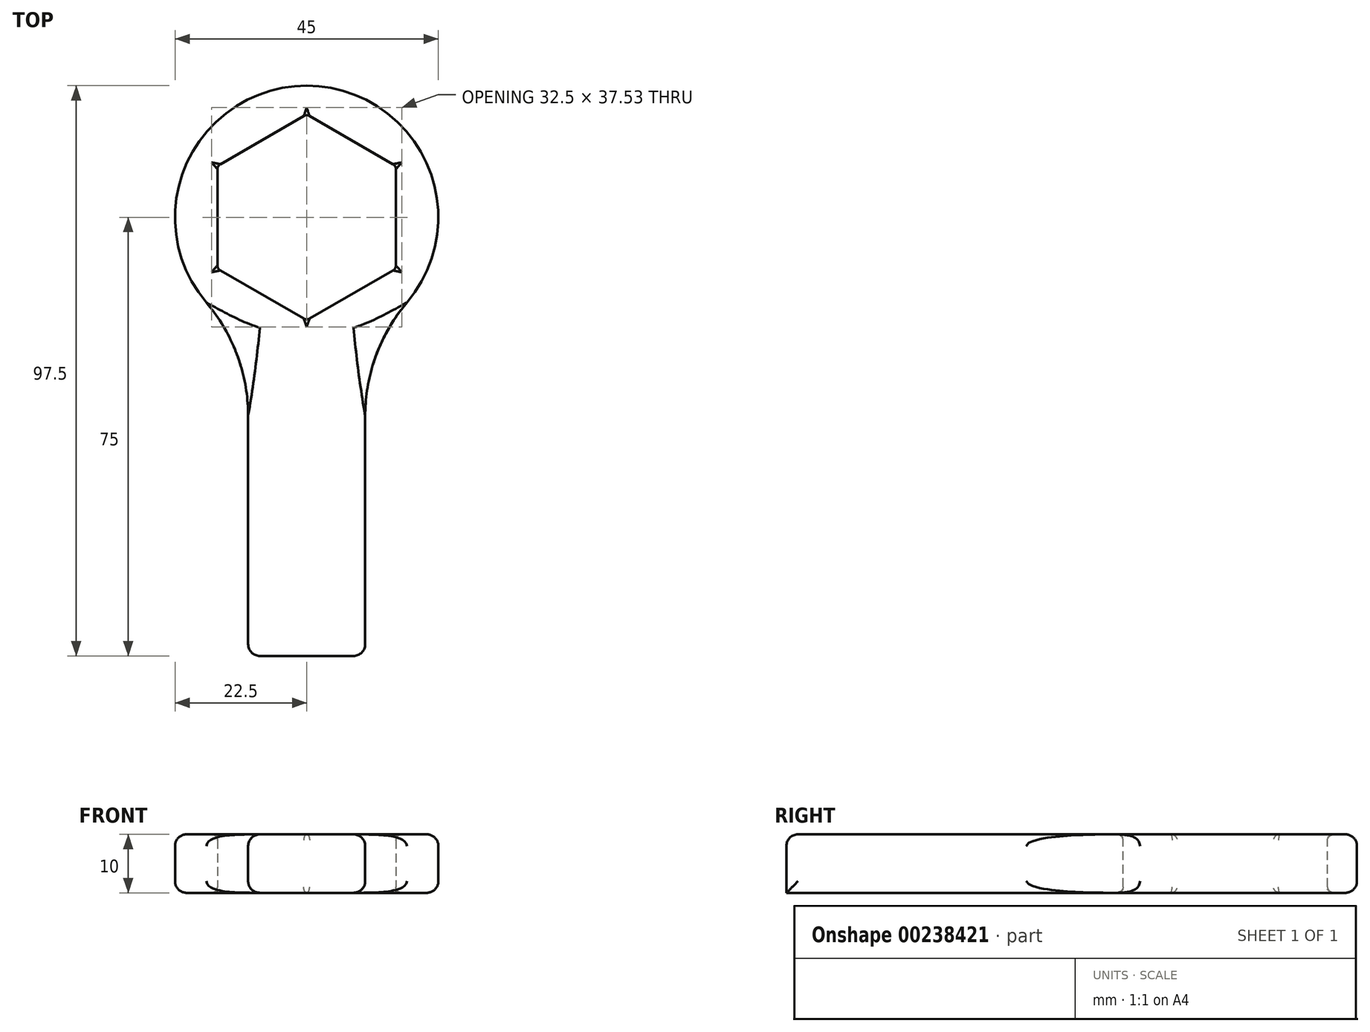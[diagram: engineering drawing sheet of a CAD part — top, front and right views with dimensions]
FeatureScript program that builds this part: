
annotation { "Feature Type Name" : "Feature", "Feature Type Description" : "" }
export const myFeature = defineFeature(function(context is Context, id is Id, definition is map)
    precondition{}
    {
        {
            var Q0;
            Q0=qCreatedBy(makeId("Top.planeOp"),FACE);
            var sketch = newSketch(context, id + "F0", { "sketchPlane" : qUnion([Q0])});
            skCircle(sketch, "E0.cCircle", {"center": v(0, 0) * mm, "radius": 15.25 * mm, "construction": true});
            skLineSegment(sketch, "E0.0", {"start": v(15.25, 8.8) * mm, "end": v(15.25, -8.8) * mm});
            skLineSegment(sketch, "E0.1", {"start": v(15.25, -8.8) * mm, "end": v(0, -17.6) * mm});
            skLineSegment(sketch, "E0.2", {"start": v(0, -17.6) * mm, "end": v(-15.25, -8.8) * mm});
            skLineSegment(sketch, "E0.3", {"start": v(-15.25, -8.8) * mm, "end": v(-15.25, 8.8) * mm});
            skLineSegment(sketch, "E0.4", {"start": v(-15.25, 8.8) * mm, "end": v(0, 17.6) * mm});
            skLineSegment(sketch, "E0.5", {"start": v(0, 17.6) * mm, "end": v(15.25, 8.8) * mm});
            skPoint(sketch, "E0.0.midPoint", {"position": v(15.25, 0) * mm});
            skCircle(sketch, "E1", {"center": v(0, 0) * mm, "radius": 22.5 * mm});
            skLineSegment(sketch, "E2.bottom", {"start": v(10, -75) * mm, "end": v(-10, -75) * mm});
            skLineSegment(sketch, "E2.top", {"start": v(10, 75) * mm, "end": v(-10, 75) * mm});
            skLineSegment(sketch, "E2.left", {"start": v(10, -75) * mm, "end": v(10, 75) * mm});
            skLineSegment(sketch, "E2.right", {"start": v(-10, -75) * mm, "end": v(-10, 75) * mm});
            skSolve(sketch);
        }
        {
            var Q0;
            {var subQ5=sQuery(id+"F0.wireOp",EDGE,"E2.bottom");Q0=makeQuery(id+"F0.imprint","IMPRINT",FACE,{"disambiguationData":[TD([[makeQuery(id+"F0.imprint","IMPRINT",EDGE,{"derivedFrom":subQ5}),-1.0]])]});}
            var Q1;
            {var subQ5=sQuery(id+"F0.wireOp",EDGE,"E0.0");Q1=makeQuery(id+"F0.imprint","IMPRINT",FACE,{"disambiguationData":[TD([[makeQuery(id+"F0.imprint","IMPRINT",EDGE,{"derivedFrom":subQ5}),1.0]])]});}
            var Q2;
            {var subQ7=sQuery(id+"F0.wireOp",EDGE,"E0.3");Q2=makeQuery(id+"F0.imprint","IMPRINT",FACE,{"disambiguationData":[TD([[makeQuery(id+"F0.imprint","IMPRINT",EDGE,{"derivedFrom":subQ7}),1.0]])]});}
            var Q3;
            {var subQ0=sQuery(id+"F0.wireOp",EDGE,"E0.2");var subQ1=sQuery(id+"F0.wireOp",EDGE,"E0.1");var subQ2=makeQuery(id+"F0.imprint","INTERSECT",VERTEX,{"derivedFrom":[subQ1,subQ0]});Q3=makeQuery(id+"F0.imprint","IMPRINT",FACE,{"disambiguationData":[TD([[makeQuery(id+"F0.imprint","IMPRINT",EDGE,{"disambiguationData":[TD([[subQ2,1.0]])],"derivedFrom":subQ1}),1.0]])]});}
            var Q4;
            {var subQ3=sQuery(id+"F0.wireOp",EDGE,"E0.5");var subQ5=sQuery(id+"F0.wireOp",EDGE,"E0.4");var subQ6=makeQuery(id+"F0.imprint","INTERSECT",VERTEX,{"derivedFrom":[subQ5,subQ3]});Q4=makeQuery(id+"F0.imprint","IMPRINT",FACE,{"disambiguationData":[TD([[makeQuery(id+"F0.imprint","IMPRINT",EDGE,{"disambiguationData":[TD([[subQ6,1.0]])],"derivedFrom":subQ5}),1.0]])]});}
            extrude(context, id + "F1", {"entities" : qUnion([Q0, Q1, Q2, Q3, Q4]), "depth" : 10 * mm, "offsetDistance" : 25 * mm});
        }
        {
            var Q0;
            Q0=makeQuery(id+"F1.opExtrude","CAP_EDGE",EDGE,{"disambiguationData":[OSD([sQuery(id+"F0.wireOp",EDGE,"E2.right")])],"isStart":false});
            var Q1;
            Q1=makeQuery(id+"F1.opExtrude","CAP_EDGE",EDGE,{"disambiguationData":[OSD([sQuery(id+"F0.wireOp",EDGE,"E2.left")])],"isStart":false});
            var Q2;
            Q2=makeQuery(id+"F1.opExtrude","CAP_EDGE",EDGE,{"disambiguationData":[OSD([sQuery(id+"F0.wireOp",EDGE,"E2.bottom")])],"isStart":false});
            var Q3;
            Q3=makeQuery(id+"F1.opExtrude","SWEPT_EDGE",EDGE,{"disambiguationData":[OSD([sQuery(id+"F0.wireOp",EDGE,"E2.bottom"),sQuery(id+"F0.wireOp",EDGE,"E2.right")])]});
            var Q4;
            Q4=makeQuery(id+"F1.opExtrude","SWEPT_EDGE",EDGE,{"disambiguationData":[OSD([sQuery(id+"F0.wireOp",EDGE,"E2.bottom"),sQuery(id+"F0.wireOp",EDGE,"E2.left")])]});
            var Q5;
            Q5=makeQuery(id+"F1.opExtrude","CAP_EDGE",EDGE,{"disambiguationData":[OSD([sQuery(id+"F0.wireOp",EDGE,"E2.right")])],"isStart":true});
            var Q6;
            Q6=makeQuery(id+"F1.opExtrude","CAP_EDGE",EDGE,{"disambiguationData":[OSD([sQuery(id+"F0.wireOp",EDGE,"E2.left")])],"isStart":true});
            fillet(context, id + "F2", {"entities" : qUnion([Q0, Q1, Q2, Q3, Q4, Q5, Q6]), "radius" : 2 * mm, "allowEdgeOverflow" : false});
        }
        {
            var Q0;
            Q0=makeQuery(id+"F1.opExtrude","CAP_EDGE",EDGE,{"disambiguationData":[OSD([sQuery(id+"F0.wireOp",EDGE,"E1")])],"isStart":false});
            var Q1;
            Q1=makeQuery(id+"F1.opExtrude","CAP_EDGE",EDGE,{"disambiguationData":[OSD([sQuery(id+"F0.wireOp",EDGE,"E1")])],"isStart":true});
            fillet(context, id + "F3", {"entities" : qUnion([Q0, Q1]), "radius" : 2 * mm, "tangentPropagation" : true, "allowEdgeOverflow" : false});
        }
        {
            var Q0;
            Q0=makeQuery(id+"F1.opExtrude","CAP_EDGE",EDGE,{"disambiguationData":[OSD([sQuery(id+"F0.wireOp",EDGE,"E0.3")])],"isStart":false});
            var Q1;
            Q1=makeQuery(id+"F1.opExtrude","CAP_EDGE",EDGE,{"disambiguationData":[OSD([sQuery(id+"F0.wireOp",EDGE,"E0.3")])],"isStart":true});
            var Q2;
            Q2=makeQuery(id+"F1.opExtrude","CAP_EDGE",EDGE,{"disambiguationData":[OSD([sQuery(id+"F0.wireOp",EDGE,"E0.4")])],"isStart":true});
            var Q3;
            Q3=makeQuery(id+"F1.opExtrude","CAP_EDGE",EDGE,{"disambiguationData":[OSD([sQuery(id+"F0.wireOp",EDGE,"E0.4")])],"isStart":false});
            var Q4;
            Q4=makeQuery(id+"F1.opExtrude","CAP_EDGE",EDGE,{"disambiguationData":[OSD([sQuery(id+"F0.wireOp",EDGE,"E0.5")])],"isStart":false});
            var Q5;
            Q5=makeQuery(id+"F1.opExtrude","CAP_EDGE",EDGE,{"disambiguationData":[OSD([sQuery(id+"F0.wireOp",EDGE,"E0.5")])],"isStart":true});
            var Q6;
            Q6=makeQuery(id+"F1.opExtrude","CAP_EDGE",EDGE,{"disambiguationData":[OSD([sQuery(id+"F0.wireOp",EDGE,"E0.0")])],"isStart":false});
            var Q7;
            Q7=makeQuery(id+"F1.opExtrude","CAP_EDGE",EDGE,{"disambiguationData":[OSD([sQuery(id+"F0.wireOp",EDGE,"E0.0")])],"isStart":true});
            var Q8;
            Q8=makeQuery(id+"F1.opExtrude","CAP_EDGE",EDGE,{"disambiguationData":[OSD([sQuery(id+"F0.wireOp",EDGE,"E0.1")])],"isStart":false});
            var Q9;
            Q9=makeQuery(id+"F1.opExtrude","CAP_EDGE",EDGE,{"disambiguationData":[OSD([sQuery(id+"F0.wireOp",EDGE,"E0.1")])],"isStart":true});
            var Q10;
            Q10=makeQuery(id+"F1.opExtrude","CAP_EDGE",EDGE,{"disambiguationData":[OSD([sQuery(id+"F0.wireOp",EDGE,"E0.2")])],"isStart":false});
            var Q11;
            Q11=makeQuery(id+"F1.opExtrude","CAP_EDGE",EDGE,{"disambiguationData":[OSD([sQuery(id+"F0.wireOp",EDGE,"E0.2")])],"isStart":true});
            fillet(context, id + "F4", {"entities" : qUnion([Q0, Q1, Q2, Q3, Q4, Q5, Q6, Q7, Q8, Q9, Q10, Q11]), "radius" : 1 * mm, "tangentPropagation" : true, "allowEdgeOverflow" : false});
        }
        {
            var Q0;
            Q0=makeQuery(id+"F1.opExtrude","SWEPT_EDGE",EDGE,{"disambiguationData":[OSD([sQuery(id+"F0.wireOp",EDGE,"E0.4"),sQuery(id+"F0.wireOp",EDGE,"E0.5")])]});
            var Q1;
            Q1=makeQuery(id+"F1.opExtrude","SWEPT_EDGE",EDGE,{"disambiguationData":[OSD([sQuery(id+"F0.wireOp",EDGE,"E0.3"),sQuery(id+"F0.wireOp",EDGE,"E0.4")])]});
            var Q2;
            Q2=makeQuery(id+"F1.opExtrude","SWEPT_EDGE",EDGE,{"disambiguationData":[OSD([sQuery(id+"F0.wireOp",EDGE,"E0.2"),sQuery(id+"F0.wireOp",EDGE,"E0.3")])]});
            var Q3;
            Q3=makeQuery(id+"F1.opExtrude","SWEPT_EDGE",EDGE,{"disambiguationData":[OSD([sQuery(id+"F0.wireOp",EDGE,"E0.1"),sQuery(id+"F0.wireOp",EDGE,"E0.2")])]});
            var Q4;
            Q4=makeQuery(id+"F1.opExtrude","SWEPT_EDGE",EDGE,{"disambiguationData":[OSD([sQuery(id+"F0.wireOp",EDGE,"E0.0"),sQuery(id+"F0.wireOp",EDGE,"E0.1")])]});
            var Q5;
            Q5=makeQuery(id+"F1.opExtrude","SWEPT_EDGE",EDGE,{"disambiguationData":[OSD([sQuery(id+"F0.wireOp",EDGE,"E0.0"),sQuery(id+"F0.wireOp",EDGE,"E0.5")])]});
            fillet(context, id + "F5", {"entities" : qUnion([Q0, Q1, Q2, Q3, Q4, Q5]), "radius" : 1 * mm, "tangentPropagation" : true, "allowEdgeOverflow" : false});
        }
        {
            var Q0;
            Q0=makeQuery(id+"F1.opExtrude","SWEPT_EDGE",EDGE,{"disambiguationData":[OSD([sQuery(id+"F0.wireOp",EDGE,"E1"),sQuery(id+"F0.wireOp",EDGE,"E2.left")])]});
            var Q1;
            Q1=makeQuery(id+"F1.opExtrude","SWEPT_EDGE",EDGE,{"disambiguationData":[OSD([sQuery(id+"F0.wireOp",EDGE,"E1"),sQuery(id+"F0.wireOp",EDGE,"E2.right")])]});
            fillet(context, id + "F6", {"entities" : qUnion([Q0, Q1]), "radius" : 30 * mm, "tangentPropagation" : true, "allowEdgeOverflow" : false});
        }
    });
